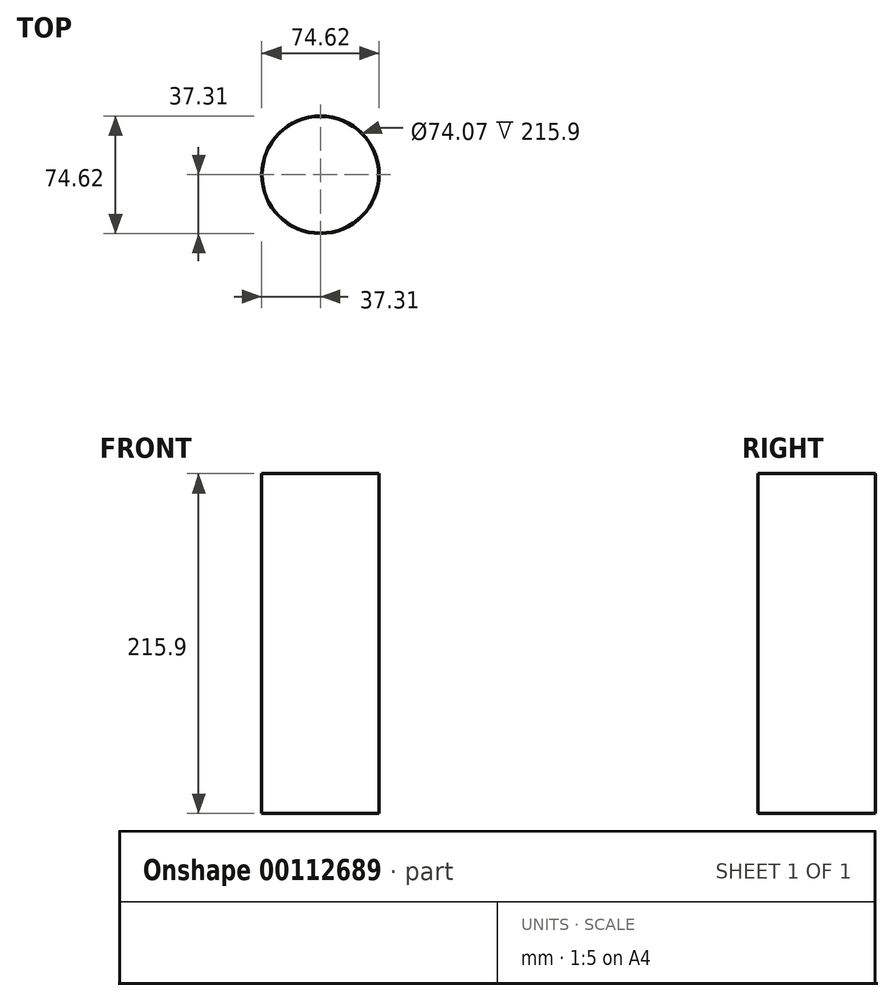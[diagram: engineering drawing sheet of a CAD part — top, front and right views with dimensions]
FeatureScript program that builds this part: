
annotation { "Feature Type Name" : "Feature", "Feature Type Description" : "" }
export const myFeature = defineFeature(function(context is Context, id is Id, definition is map)
    precondition{}
    {
        {
            var Q0;
            Q0=qCreatedBy(makeId("Top.planeOp"),FACE);
            var sketch = newSketch(context, id + "F0", { "sketchPlane" : qUnion([Q0])});
            skCircle(sketch, "E0", {"center": v(0, 0) * mm, "radius": 37.31 * mm});
            skCircle(sketch, "E1", {"center": v(0, 0) * mm, "radius": 37.03 * mm});
            skSolve(sketch);
        }
        {
            var Q0;
            Q0 = qSketchRegion(id + "F0", true);
            extrude(context, id + "F1", {"entities" : qUnion([Q0]), "depth" : 215.9 * mm});
        }
    });
